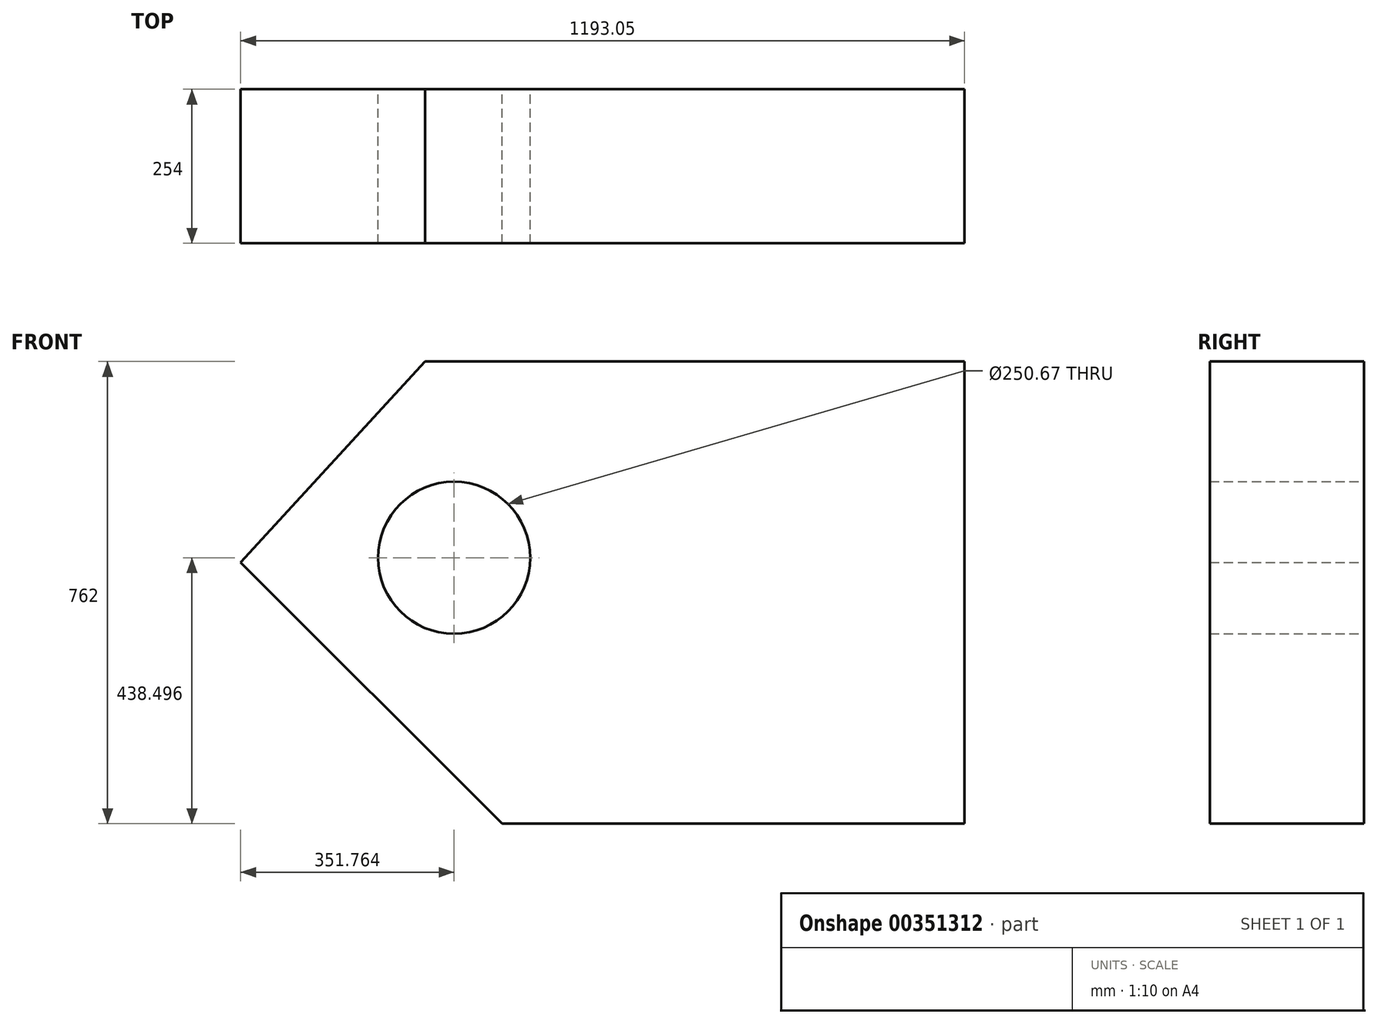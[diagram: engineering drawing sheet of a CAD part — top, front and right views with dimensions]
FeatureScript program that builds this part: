
annotation { "Feature Type Name" : "Feature", "Feature Type Description" : "" }
export const myFeature = defineFeature(function(context is Context, id is Id, definition is map)
    precondition{}
    {
        {
            var Q0;
            Q0=qCreatedBy(makeId("Front.planeOp"),FACE);
            var sketch = newSketch(context, id + "F0", { "sketchPlane" : qUnion([Q0])});
            skLineSegment(sketch, "E0", {"start": v(0, 0) * mm, "end": v(431.05, -431.05) * mm});
            skLineSegment(sketch, "E1", {"start": v(431.05, -431.05) * mm, "end": v(1193.05, -431.05) * mm});
            skLineSegment(sketch, "E2", {"start": v(1193.05, -431.05) * mm, "end": v(1193.05, 330.95) * mm});
            skLineSegment(sketch, "E3", {"start": v(1193.05, 330.95) * mm, "end": v(304.05, 330.95) * mm});
            skLineSegment(sketch, "E4", {"start": v(304.05, 330.95) * mm, "end": v(0, 0) * mm});
            skCircle(sketch, "E5", {"center": v(351.76, 7.45) * mm, "radius": 125.33 * mm});
            skSolve(sketch);
        }
        {
            var Q0;
            Q0 = qSketchRegion(id + "F0", true);
            extrude(context, id + "F1", {"entities" : qUnion([Q0]), "depth" : 254 * mm});
        }
    });
